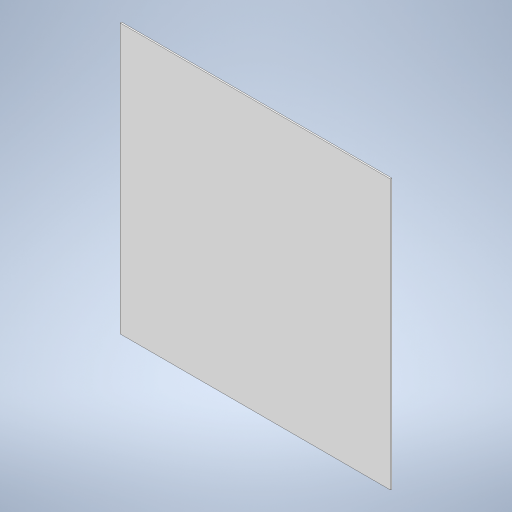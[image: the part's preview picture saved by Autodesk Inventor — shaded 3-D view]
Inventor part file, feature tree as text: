
AUTODESK INVENTOR PART (.ipt)
format: ipt  version: 2023 (Build 270158000, 158)  size: 194,048 bytes
history: native  units: mm
features: extrude x1, sketch x1
ambient origin geometry x8: Origin, YZ Plane, XZ Plane, XY Plane, X Axis, Y Axis, Z Axis, Center Point
bodies: Solid1 (feature_tree)
feature tree (2):
  extrude  "Extrusion1"  Depth=540.0mm
  sketch  "Sketch1"  dims[d0=542.0mm d1=540.0mm d2=3.0mm d3=0.0mm]
